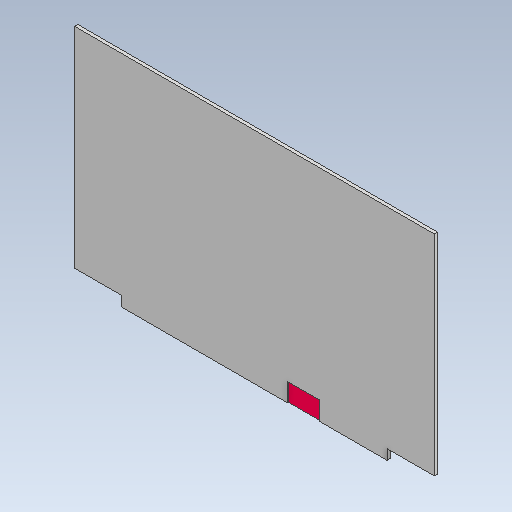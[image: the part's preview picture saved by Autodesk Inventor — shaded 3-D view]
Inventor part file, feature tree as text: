
AUTODESK INVENTOR PART (.ipt)
format: ipt  version: 2021.2 (Build 252289000, 289)  size: 180,224 bytes
history: native  units: mm
features: extrude x4, sketch x4, projected_geometry x3, other x1
ambient origin geometry x8: Origin, YZ Plane, XZ Plane, XY Plane, X Axis, Y Axis, Z Axis, Center Point
bodies: Body1 (feature_tree)
feature tree (12):
  other  "Твердое тело1"
  extrude  "Выдавливание1"  Depth=390.0mm
  extrude  "Выдавливание2"  Depth=227.0mm
  extrude  "Выдавливание3"  Depth=382.0mm
  extrude  "Выдавливание4"  Depth=215.0mm
  sketch  "Эскиз1"
  sketch  "Эскиз2"
  projected_geometry  "Спроецированная петля1"
  sketch  "Эскиз3"
  projected_geometry  "Спроецированная петля2"
  sketch  "Эскиз5"
  projected_geometry  "Спроецированная петля3"
